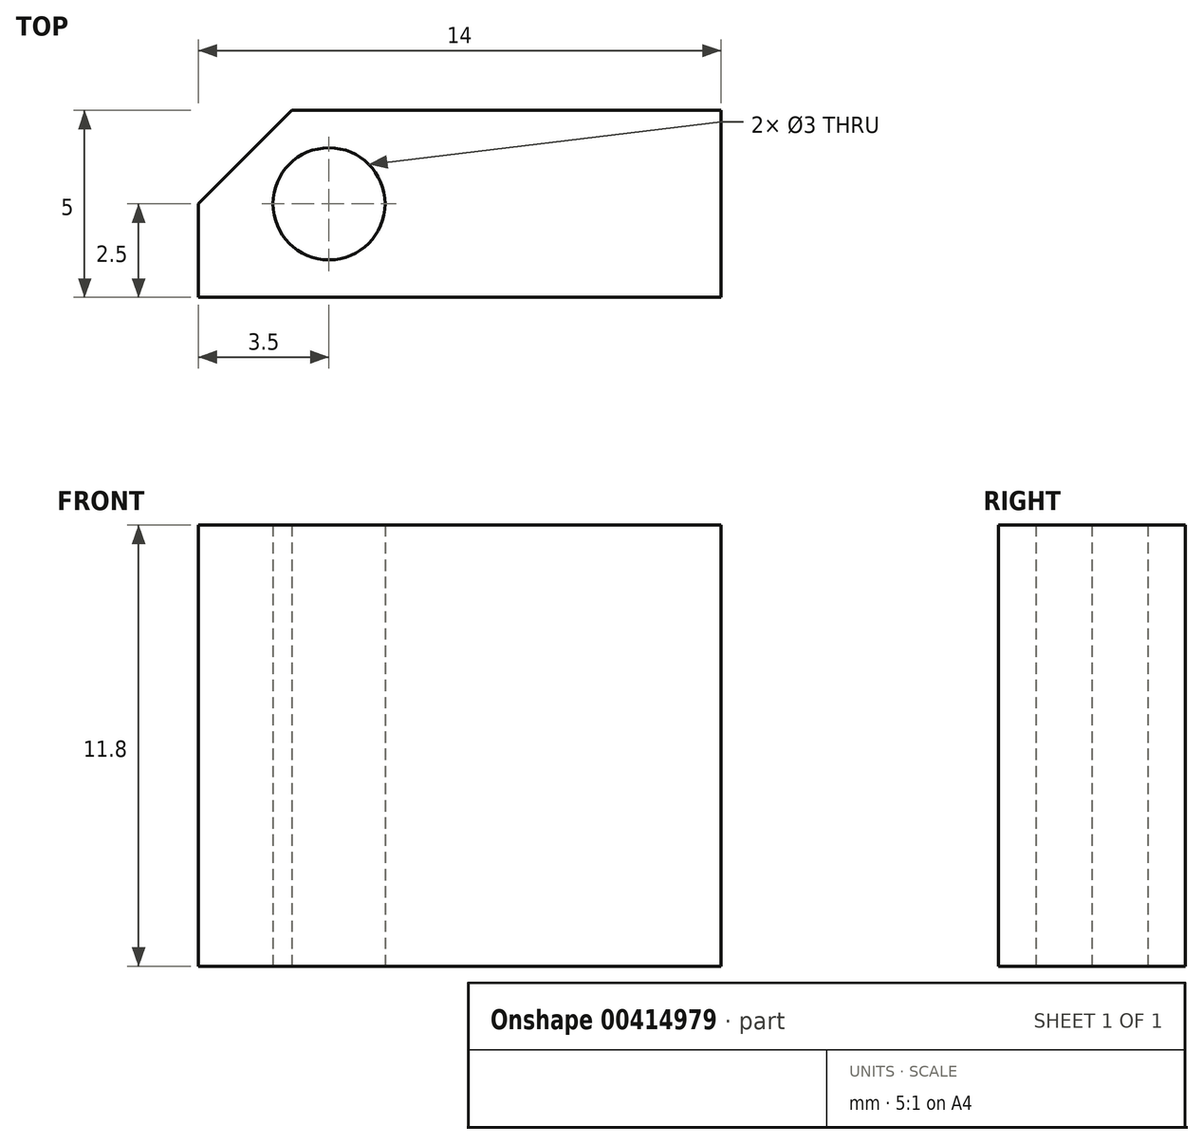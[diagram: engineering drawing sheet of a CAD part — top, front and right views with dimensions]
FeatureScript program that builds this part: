
annotation { "Feature Type Name" : "Feature", "Feature Type Description" : "" }
export const myFeature = defineFeature(function(context is Context, id is Id, definition is map)
    precondition{}
    {
        {
            var Q0;
            Q0=qCreatedBy(makeId("Top.planeOp"),FACE);
            var sketch = newSketch(context, id + "F0", { "sketchPlane" : qUnion([Q0])});
            skLineSegment(sketch, "E0.bottom", {"start": v(0, 0) * mm, "end": v(14, 0) * mm});
            skLineSegment(sketch, "E0.top", {"start": v(2.5, 5) * mm, "end": v(14, 5) * mm});
            skLineSegment(sketch, "E0.left", {"start": v(0, 0) * mm, "end": v(0, 2.5) * mm});
            skLineSegment(sketch, "E0.right", {"start": v(14, 0) * mm, "end": v(14, 5) * mm});
            skLineSegment(sketch, "E1", {"start": v(0, 2.5) * mm, "end": v(14, 2.5) * mm, "construction": true});
            skLineSegment(sketch, "E2", {"start": v(0, 2.5) * mm, "end": v(2.5, 5) * mm});
            skPoint(sketch, "E3.orphan", {"position": v(0, 5) * mm});
            skLineSegment(sketch, "E4", {"start": v(3.5, 5) * mm, "end": v(3.5, 0) * mm, "construction": true});
            skCircle(sketch, "E5", {"center": v(3.5, 2.5) * mm, "radius": 1.5 * mm});
            skSolve(sketch);
        }
        {
            var Q0;
            Q0 = qSketchRegion(id + "F0", true);
            extrude(context, id + "F1", {"entities" : qUnion([Q0]), "depth" : 11.8 * mm});
        }
    });
